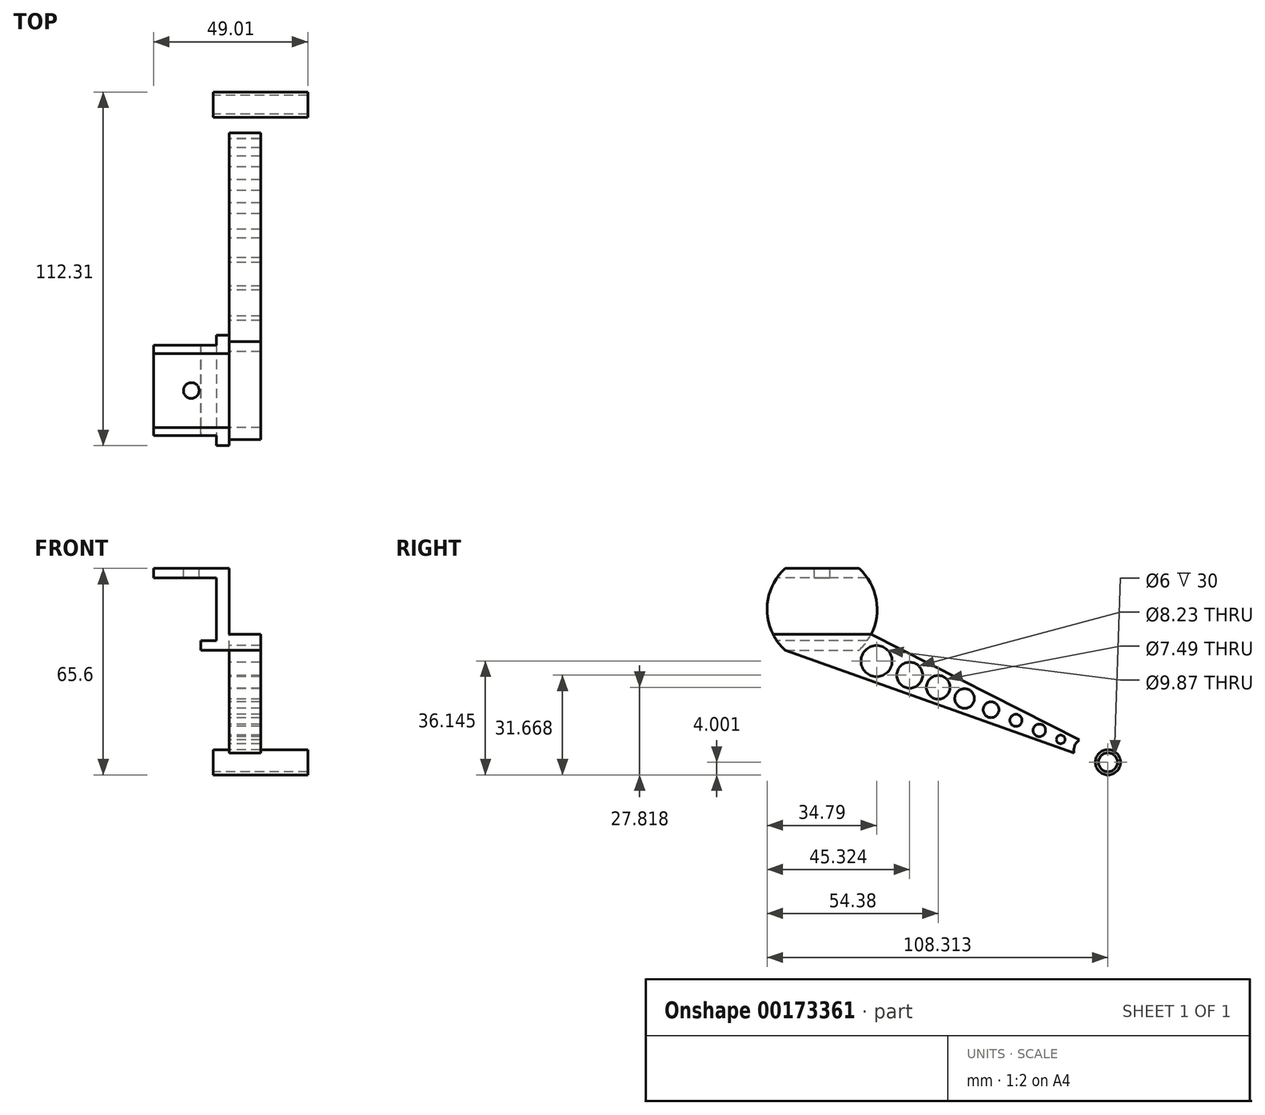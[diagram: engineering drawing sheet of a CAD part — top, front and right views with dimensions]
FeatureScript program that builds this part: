
annotation { "Feature Type Name" : "Feature", "Feature Type Description" : "" }
export const myFeature = defineFeature(function(context is Context, id is Id, definition is map)
    precondition{}
    {
        {
            var Q0;
            Q0=qCreatedBy(makeId("Right.planeOp"),FACE);
            var sketch = newSketch(context, id + "F0", { "sketchPlane" : qUnion([Q0])});
            skArc(sketch, "E0", {"start": v(-11.72, 13) * mm, "mid": v(-17.5, 0) * mm, "end": v(-11.72, -13) * mm});
            skLineSegment(sketch, "E1.0", {"start": v(11.72, 13) * mm, "end": v(-11.72, 13) * mm});
            skLineSegment(sketch, "E2.0", {"start": v(-11.72, -13) * mm, "end": v(11.72, -13) * mm});
            skArc(sketch, "E3.trimOffspring", {"start": v(11.72, -13) * mm, "mid": v(17.5, 0) * mm, "end": v(11.72, 13) * mm});
            skSolve(sketch);
        }
        {
            var Q0;
            Q0 = qSketchRegion(id + "F0", true);
            extrude(context, id + "F1", {"entities" : qUnion([Q0]), "depth" : 4 * mm});
        }
        {
            var Q0;
            Q0=makeQuery(id+"F1.opExtrude","CAP_FACE",FACE,{"disambiguationData":[OSD([sQuery(id+"F0.wireOp",EDGE,"E0"),sQuery(id+"F0.wireOp",EDGE,"E1.0"),sQuery(id+"F0.wireOp",EDGE,"E2.0"),sQuery(id+"F0.wireOp",EDGE,"E3.trimOffspring")])],"isStart":true});
            var sketch = newSketch(context, id + "F2", { "sketchPlane" : qUnion([Q0])});
            skLineSegment(sketch, "E4", {"start": v(-11.72, 13) * mm, "end": v(11.72, 13) * mm});
            skLineSegment(sketch, "E5.0", {"start": v(-14.36, 10) * mm, "end": v(14.36, 10) * mm});
            skArc(sketch, "E6", {"start": v(-11.72, 13) * mm, "mid": v(-13.12, 11.58) * mm, "end": v(-14.36, 10) * mm});
            skArc(sketch, "E7.trimOffspring", {"start": v(14.36, 10) * mm, "mid": v(13.12, 11.58) * mm, "end": v(11.72, 13) * mm});
            skSolve(sketch);
        }
        {
            var Q0;
            Q0 = qSketchRegion(id + "F2", true);
            extrude(context, id + "F3", {"entities" : qUnion([Q0]), "operationType" : NewBodyOperationType.ADD, "depth" : 20 * mm});
        }
        {
            var Q0;
            Q0=makeQuery(id+"F1.opExtrude","CAP_FACE",FACE,{"disambiguationData":[OSD([sQuery(id+"F0.wireOp",EDGE,"E0"),sQuery(id+"F0.wireOp",EDGE,"E1.0"),sQuery(id+"F0.wireOp",EDGE,"E2.0"),sQuery(id+"F0.wireOp",EDGE,"E3.trimOffspring")])],"isStart":true});
            var sketch = newSketch(context, id + "F4", { "sketchPlane" : qUnion([Q0])});
            skLineSegment(sketch, "E8", {"start": v(-11.72, -13) * mm, "end": v(11.72, -13) * mm});
            skLineSegment(sketch, "E9.0", {"start": v(-14.36, -10) * mm, "end": v(14.36, -10) * mm});
            skArc(sketch, "E10", {"start": v(-14.36, -10) * mm, "mid": v(-13.12, -11.58) * mm, "end": v(-11.72, -13) * mm});
            skArc(sketch, "E11.trimOffspring", {"start": v(11.72, -13) * mm, "mid": v(13.12, -11.58) * mm, "end": v(14.36, -10) * mm});
            skSolve(sketch);
        }
        {
            var Q0;
            Q0 = qSketchRegion(id + "F4", true);
            extrude(context, id + "F5", {"entities" : qUnion([Q0]), "operationType" : NewBodyOperationType.ADD, "depth" : 5 * mm});
        }
        {
            var Q0;
            Q0=makeQuery(id+"F3.boolean.opBoolean","MERGE",FACE,{"derivedFrom":[makeQuery(id+"F1.opExtrude","SWEPT_FACE",FACE,{"disambiguationData":[OSD([sQuery(id+"F0.wireOp",EDGE,"E1.0")])]}),makeQuery(id+"F3.opExtrude","SWEPT_FACE",FACE,{"disambiguationData":[OSD([sQuery(id+"F2.wireOp",EDGE,"E4")])]})]});
            var sketch = newSketch(context, id + "F6", { "sketchPlane" : qUnion([Q0])});
            skCircle(sketch, "E12", {"center": v(-8, 0) * mm, "radius": 2.5 * mm});
            skPoint(sketch, "E12.centerSnap0", {"position": v(-20, 0) * mm});
            skPoint(sketch, "E12.centerSnap1", {"position": v(-8, 11.72) * mm});
            skSolve(sketch);
        }
        {
            var Q0;
            Q0 = qSketchRegion(id + "F6", true);
            extrude(context, id + "F7", {"entities" : qUnion([Q0]), "operationType" : NewBodyOperationType.REMOVE, "oppositeDirection" : true, "depth" : 5 * mm});
        }
        {
            var Q0;
            Q0=makeQuery(id+"F1.opExtrude","CAP_FACE",FACE,{"disambiguationData":[OSD([sQuery(id+"F0.wireOp",EDGE,"E0"),sQuery(id+"F0.wireOp",EDGE,"E1.0"),sQuery(id+"F0.wireOp",EDGE,"E2.0"),sQuery(id+"F0.wireOp",EDGE,"E3.trimOffspring")])],"isStart":false});
            var sketch = newSketch(context, id + "F8", { "sketchPlane" : qUnion([Q0])});
            skLineSegment(sketch, "E13", {"start": v(-11.72, -13) * mm, "end": v(11.72, -13) * mm});
            skLineSegment(sketch, "E14.0", {"start": v(-15.56, -8) * mm, "end": v(15.56, -8) * mm});
            skArc(sketch, "E15", {"start": v(-15.56, -8) * mm, "mid": v(-13.87, -10.67) * mm, "end": v(-11.72, -13) * mm});
            skArc(sketch, "E16.trimOffspring", {"start": v(11.72, -13) * mm, "mid": v(13.87, -10.67) * mm, "end": v(15.56, -8) * mm});
            skSolve(sketch);
        }
        {
            var Q0;
            Q0 = qSketchRegion(id + "F8", true);
            extrude(context, id + "F9", {"entities" : qUnion([Q0]), "operationType" : NewBodyOperationType.ADD, "depth" : 0.01 * mm});
        }
        {
            var Q0;
            Q0=makeQuery(id+"F9.opExtrude","CAP_FACE",FACE,{"disambiguationData":[OSD([sQuery(id+"F8.wireOp",EDGE,"E13"),sQuery(id+"F8.wireOp",EDGE,"E14.0"),sQuery(id+"F8.wireOp",EDGE,"E15"),sQuery(id+"F8.wireOp",EDGE,"E16.trimOffspring")])],"isStart":false});
            var sketch = newSketch(context, id + "F10", { "sketchPlane" : qUnion([Q0])});
            skLineSegment(sketch, "E17", {"start": v(-11.72, -13) * mm, "end": v(11.72, -13) * mm});
            skLineSegment(sketch, "E18", {"start": v(-15.56, -8) * mm, "end": v(15.56, -8) * mm});
            skArc(sketch, "E19", {"start": v(-15.56, -8) * mm, "mid": v(-13.87, -10.67) * mm, "end": v(-11.72, -13) * mm});
            skArc(sketch, "E20.trimOffspring", {"start": v(11.72, -13) * mm, "mid": v(13.87, -10.67) * mm, "end": v(15.56, -8) * mm});
            skLineSegment(sketch, "E21", {"start": v(-11.72, -13) * mm, "end": v(80.07, -45.65) * mm});
            skLineSegment(sketch, "E22", {"start": v(15.56, -8) * mm, "end": v(81.78, -41.45) * mm});
            skCircle(sketch, "E23", {"center": v(17.3, -16.45) * mm, "radius": 4.93 * mm});
            skCircle(sketch, "E24", {"center": v(27.82, -20.93) * mm, "radius": 4.12 * mm});
            skCircle(sketch, "E25", {"center": v(36.88, -24.78) * mm, "radius": 3.74 * mm});
            skCircle(sketch, "E26", {"center": v(45.27, -28.35) * mm, "radius": 3.11 * mm});
            skCircle(sketch, "E27", {"center": v(53.66, -31.92) * mm, "radius": 2.5 * mm});
            skCircle(sketch, "E28", {"center": v(61.56, -35.27) * mm, "radius": 1.92 * mm});
            skCircle(sketch, "E29", {"center": v(69.01, -38.44) * mm, "radius": 1.99 * mm});
            skCircle(sketch, "E30", {"center": v(75.8, -41.33) * mm, "radius": 1.37 * mm});
            skArc(sketch, "E31", {"start": v(81.78, -41.45) * mm, "mid": v(80.27, -43.29) * mm, "end": v(80.07, -45.65) * mm});
            skPoint(sketch, "E32.orphan", {"position": v(83.98, -47.04) * mm});
            skPoint(sketch, "E33.orphan", {"position": v(83.98, -42.56) * mm});
            skSolve(sketch);
        }
        {
            var Q0;
            Q0 = qSketchRegion(id + "F10", true);
            extrude(context, id + "F11", {"entities" : qUnion([Q0]), "operationType" : NewBodyOperationType.ADD, "depth" : 10 * mm});
        }
        {
            var Q0;
            Q0=makeQuery(id+"F11.opExtrude","CAP_FACE",FACE,{"disambiguationData":[OSD([sQuery(id+"F10.wireOp",EDGE,"E18"),sQuery(id+"F10.wireOp",EDGE,"E19"),sQuery(id+"F10.wireOp",EDGE,"E20.trimOffspring"),sQuery(id+"F10.wireOp",EDGE,"E21"),sQuery(id+"F10.wireOp",EDGE,"yEHkmcCr-NKS1-WiRE-sP3y-5vzrxHRfFTSi")])],"isStart":false});
            var sketch = newSketch(context, id + "F12", { "sketchPlane" : qUnion([Q0])});
            skCircle(sketch, "E34", {"center": v(90.81, -48.6) * mm, "radius": 4 * mm});
            skCircle(sketch, "E35", {"center": v(90.81, -48.6) * mm, "radius": 3 * mm});
            skSolve(sketch);
        }
        {
            var Q0;
            Q0 = qSketchRegion(id + "F12", true);
            extrude(context, id + "F13", {"entities" : qUnion([Q0]), "operationType" : NewBodyOperationType.ADD, "depth" : 15 * mm, "hasSecondDirection" : true, "secondDirectionOppositeDirection" : true, "secondDirectionDepth" : 15 * mm});
        }
        {
            var Q0;
            Q0=makeQuery(id+"F13.opExtrude","CAP_FACE",FACE,{"disambiguationData":[OSD([sQuery(id+"F12.wireOp",EDGE,"E34"),sQuery(id+"F12.wireOp",EDGE,"E35")])],"isStart":false});
            var sketch = newSketch(context, id + "F14", { "sketchPlane" : qUnion([Q0])});
            skCircle(sketch, "E36", {"center": v(90.81, -48.6) * mm, "radius": 2.5 * mm});
            skSolve(sketch);
        }
        {
            var Q0;
            Q0 = qSketchRegion(id + "F14", true);
            extrude(context, id + "F15", {"entities" : qUnion([Q0]), "operationType" : NewBodyOperationType.REMOVE, "oppositeDirection" : true, "depth" : 25 * mm});
        }
    });
